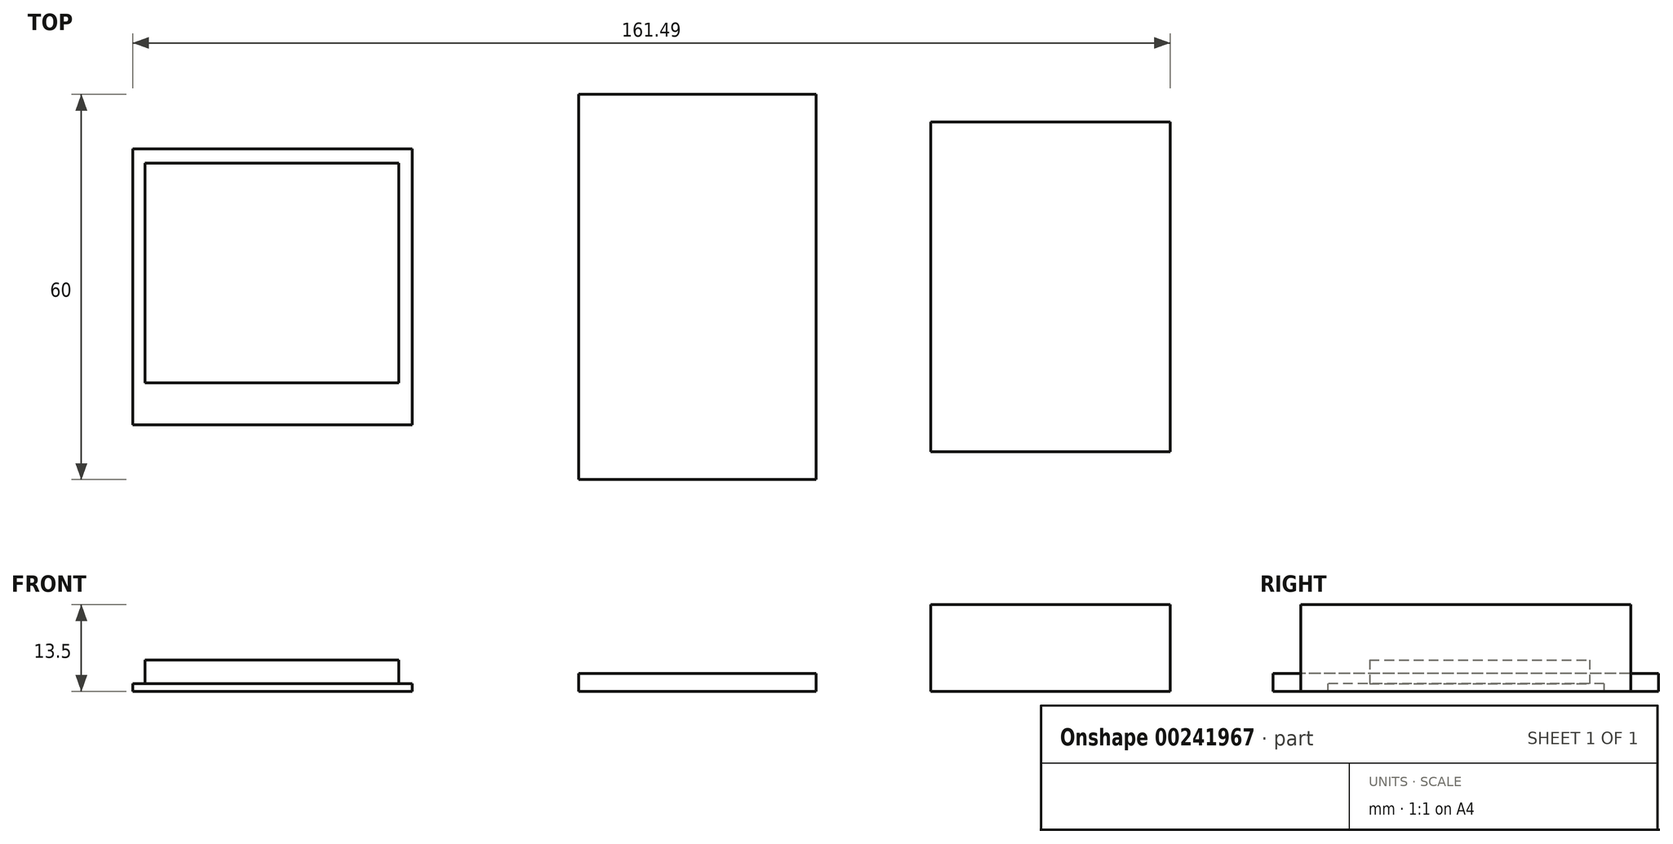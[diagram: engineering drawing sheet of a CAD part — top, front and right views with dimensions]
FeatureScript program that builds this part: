
annotation { "Feature Type Name" : "Feature", "Feature Type Description" : "" }
export const myFeature = defineFeature(function(context is Context, id is Id, definition is map)
    precondition{}
    {
        {
            var Q0;
            Q0=qCreatedBy(makeId("Top.planeOp"),FACE);
            var sketch = newSketch(context, id + "F0", { "sketchPlane" : qUnion([Q0])});
            skLineSegment(sketch, "E0.bottom", {"start": v(-18.5, 30) * mm, "end": v(18.5, 30) * mm});
            skLineSegment(sketch, "E0.top", {"start": v(-18.5, -30) * mm, "end": v(18.5, -30) * mm});
            skLineSegment(sketch, "E0.left", {"start": v(-18.5, 30) * mm, "end": v(-18.5, -30) * mm});
            skLineSegment(sketch, "E0.right", {"start": v(18.5, 30) * mm, "end": v(18.5, -30) * mm});
            skPoint(sketch, "E0.middle", {"position": v(0, 0) * mm});
            skSolve(sketch);
        }
        {
            var Q0;
            Q0 = qSketchRegion(id + "F0", true);
            extrude(context, id + "F1", {"entities" : qUnion([Q0]), "depth" : 2.8 * mm});
        }
        {
            var Q0;
            Q0=qCreatedBy(makeId("Top.planeOp"),FACE);
            var sketch = newSketch(context, id + "F2", { "sketchPlane" : qUnion([Q0])});
            skLineSegment(sketch, "E1.bottom", {"start": v(-44.38, 21.5) * mm, "end": v(-87.88, 21.5) * mm});
            skLineSegment(sketch, "E1.top", {"start": v(-44.38, -21.5) * mm, "end": v(-87.88, -21.5) * mm});
            skLineSegment(sketch, "E1.left", {"start": v(-44.38, 21.5) * mm, "end": v(-44.38, -21.5) * mm});
            skLineSegment(sketch, "E1.right", {"start": v(-87.88, 21.5) * mm, "end": v(-87.88, -21.5) * mm});
            skPoint(sketch, "E1.middle", {"position": v(-66.13, 0) * mm});
            skSolve(sketch);
        }
        {
            var Q0;
            Q0 = qSketchRegion(id + "F2", true);
            extrude(context, id + "F3", {"entities" : qUnion([Q0]), "depth" : 1.2 * mm});
        }
        {
            var Q0;
            Q0=qCreatedBy(makeId("Top.planeOp"),FACE);
            var sketch = newSketch(context, id + "F4", { "sketchPlane" : qUnion([Q0])});
            skLineSegment(sketch, "E2.bottom", {"start": v(36.35, 25.7) * mm, "end": v(73.6, 25.7) * mm});
            skLineSegment(sketch, "E2.top", {"start": v(36.35, -25.7) * mm, "end": v(73.6, -25.7) * mm});
            skLineSegment(sketch, "E2.left", {"start": v(36.35, 25.7) * mm, "end": v(36.35, -25.7) * mm});
            skLineSegment(sketch, "E2.right", {"start": v(73.6, 25.7) * mm, "end": v(73.6, -25.7) * mm});
            skPoint(sketch, "E2.middle", {"position": v(54.98, 0) * mm});
            skSolve(sketch);
        }
        {
            var Q0;
            Q0 = qSketchRegion(id + "F4", true);
            extrude(context, id + "F5", {"entities" : qUnion([Q0]), "depth" : 13.5 * mm});
        }
        {
            var Q0;
            Q0=makeQuery(id+"F3.opExtrude","CAP_FACE",FACE,{"disambiguationData":[OSD([sQuery(id+"F2.wireOp",EDGE,"E1.bottom"),sQuery(id+"F2.wireOp",EDGE,"E1.top"),sQuery(id+"F2.wireOp",EDGE,"E1.left"),sQuery(id+"F2.wireOp",EDGE,"E1.right")])],"isStart":false});
            var sketch = newSketch(context, id + "F6", { "sketchPlane" : qUnion([Q0])});
            skLineSegment(sketch, "E3.bottom", {"start": v(-86, -14.97) * mm, "end": v(-46.5, -14.97) * mm});
            skLineSegment(sketch, "E3.top", {"start": v(-86, 19.28) * mm, "end": v(-46.5, 19.28) * mm});
            skLineSegment(sketch, "E3.left", {"start": v(-86, -14.97) * mm, "end": v(-86, 19.28) * mm});
            skLineSegment(sketch, "E3.right", {"start": v(-46.5, -14.97) * mm, "end": v(-46.5, 19.28) * mm});
            skPoint(sketch, "E3.middle", {"position": v(-66.26, 2.16) * mm});
            skSolve(sketch);
        }
        {
            var Q0;
            Q0 = qSketchRegion(id + "F6", true);
            extrude(context, id + "F7", {"entities" : qUnion([Q0]), "operationType" : NewBodyOperationType.ADD, "depth" : 3.7 * mm});
        }
    });
